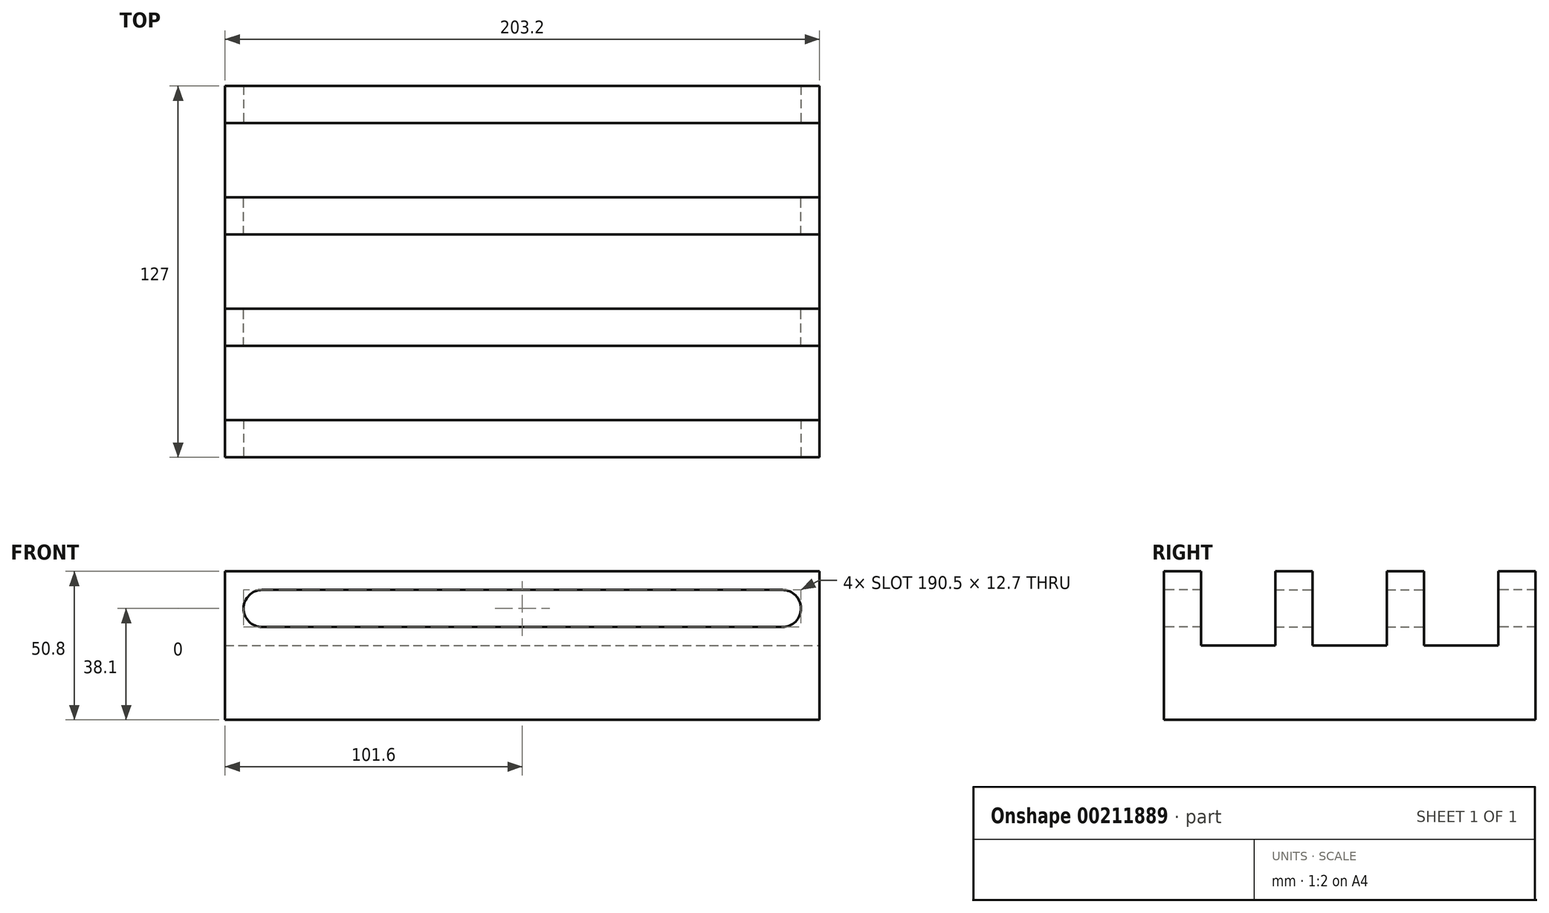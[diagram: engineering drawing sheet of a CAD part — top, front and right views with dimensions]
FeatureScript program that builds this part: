
annotation { "Feature Type Name" : "Feature", "Feature Type Description" : "" }
export const myFeature = defineFeature(function(context is Context, id is Id, definition is map)
    precondition{}
    {
        {
            var Q0;
            Q0=qCreatedBy(makeId("Top.planeOp"),FACE);
            var sketch = newSketch(context, id + "F0", { "sketchPlane" : qUnion([Q0])});
            skLineSegment(sketch, "E0.bottom", {"start": v(101.6, 63.5) * mm, "end": v(-101.6, 63.5) * mm});
            skLineSegment(sketch, "E0.top", {"start": v(101.6, -63.5) * mm, "end": v(-101.6, -63.5) * mm});
            skLineSegment(sketch, "E0.left", {"start": v(101.6, 63.5) * mm, "end": v(101.6, -63.5) * mm});
            skLineSegment(sketch, "E0.right", {"start": v(-101.6, 63.5) * mm, "end": v(-101.6, -63.5) * mm});
            skPoint(sketch, "E0.middle", {"position": v(0, 0) * mm});
            skSolve(sketch);
        }
        {
            var Q0;
            Q0 = qSketchRegion(id + "F0", true);
            extrude(context, id + "F1", {"entities" : qUnion([Q0]), "endBound" : BoundingType.SYMMETRIC, "depth" : 25.4 * mm});
        }
        {
            var Q0;
            Q0=makeQuery(id+"F1.opExtrude","CAP_FACE",FACE,{"disambiguationData":[OSD([sQuery(id+"F0.wireOp",EDGE,"E0.bottom"),sQuery(id+"F0.wireOp",EDGE,"E0.top"),sQuery(id+"F0.wireOp",EDGE,"E0.left"),sQuery(id+"F0.wireOp",EDGE,"E0.right")])],"isStart":false});
            var sketch = newSketch(context, id + "F2", { "sketchPlane" : qUnion([Q0])});
            skLineSegment(sketch, "E1.bottom", {"start": v(-101.6, 63.5) * mm, "end": v(101.6, 63.5) * mm});
            skLineSegment(sketch, "E1.top", {"start": v(-101.6, 50.8) * mm, "end": v(101.6, 50.8) * mm});
            skLineSegment(sketch, "E1.left", {"start": v(-101.6, 63.5) * mm, "end": v(-101.6, 50.8) * mm});
            skLineSegment(sketch, "E1.right", {"start": v(101.6, 63.5) * mm, "end": v(101.6, 50.8) * mm});
            skLineSegment(sketch, "E2.MirrorCS", {"start": v(-101.6, -50.8) * mm, "end": v(101.6, -50.8) * mm});
            skSolve(sketch);
        }
        {
            var Q0;
            Q0 = qSketchRegion(id + "F2", true);
            var Q1;
            {var subQ0=sQuery(id+"F2.wireOp",EDGE,"E2.MirrorCS");Q1=makeQuery(id+"F2.imprint","IMPRINT",FACE,{"disambiguationData":[TD([[makeQuery(id+"F2.imprint","IMPRINT",EDGE,{"derivedFrom":subQ0}),-1.0]])]});}
            extrude(context, id + "F3", {"entities" : qUnion([Q0, Q1]), "operationType" : NewBodyOperationType.ADD, "depth" : 25.4 * mm});
        }
        {
            var Q0;
            {var subQ0=sQuery(id+"F0.wireOp",EDGE,"E0.top");Q0=makeQuery(id+"F3.boolean.opBoolean","MERGE",FACE,{"derivedFrom":[makeQuery(id+"F1.opExtrude","SWEPT_FACE",FACE,{"disambiguationData":[OSD([subQ0])]}),makeQuery(id+"F3.opExtrude","SWEPT_FACE",FACE,{"disambiguationData":[OSD([subQ0])]})]});}
            var sketch = newSketch(context, id + "F4", { "sketchPlane" : qUnion([Q0])});
            skArc(sketch, "E3", {"start": v(88.9, 19.05) * mm, "mid": v(95.25, 25.4) * mm, "end": v(88.9, 31.75) * mm});
            skArc(sketch, "E4.MirrorC", {"start": v(-88.9, 19.05) * mm, "mid": v(-95.25, 25.4) * mm, "end": v(-88.9, 31.75) * mm});
            skLineSegment(sketch, "E5", {"start": v(88.9, 19.05) * mm, "end": v(-88.9, 19.05) * mm});
            skLineSegment(sketch, "E6", {"start": v(88.9, 31.75) * mm, "end": v(-88.9, 31.75) * mm});
            skSolve(sketch);
        }
        {
            var Q0;
            Q0 = qSketchRegion(id + "F4", true);
            extrude(context, id + "F5", {"entities" : qUnion([Q0]), "operationType" : NewBodyOperationType.REMOVE, "oppositeDirection" : true, "depth" : 127 * mm});
        }
        {
            var Q0;
            Q0=makeQuery(id+"F1.opExtrude","CAP_FACE",FACE,{"disambiguationData":[OSD([sQuery(id+"F0.wireOp",EDGE,"E0.bottom"),sQuery(id+"F0.wireOp",EDGE,"E0.top"),sQuery(id+"F0.wireOp",EDGE,"E0.left"),sQuery(id+"F0.wireOp",EDGE,"E0.right")])],"isStart":false});
            var sketch = newSketch(context, id + "F6", { "sketchPlane" : qUnion([Q0])});
            skLineSegment(sketch, "E7.bottom", {"start": v(-101.6, -25.4) * mm, "end": v(101.6, -25.4) * mm});
            skLineSegment(sketch, "E7.top", {"start": v(-101.6, -12.7) * mm, "end": v(101.6, -12.7) * mm});
            skLineSegment(sketch, "E7.left", {"start": v(-101.6, -25.4) * mm, "end": v(-101.6, -12.7) * mm});
            skLineSegment(sketch, "E7.right", {"start": v(101.6, -25.4) * mm, "end": v(101.6, -12.7) * mm});
            skLineSegment(sketch, "E8.bottom", {"start": v(-101.6, 12.7) * mm, "end": v(101.6, 12.7) * mm});
            skLineSegment(sketch, "E8.top", {"start": v(-101.6, 25.4) * mm, "end": v(101.6, 25.4) * mm});
            skLineSegment(sketch, "E8.left", {"start": v(-101.6, 12.7) * mm, "end": v(-101.6, 25.4) * mm});
            skLineSegment(sketch, "E8.right", {"start": v(101.6, 12.7) * mm, "end": v(101.6, 25.4) * mm});
            skSolve(sketch);
        }
        {
            var Q0;
            Q0=makeQuery(id+"F6.imprint","IMPRINT",FACE,{"disambiguationData":[TD([[makeQuery(id+"F6.imprint","IMPRINT",EDGE,{"derivedFrom":sQuery(id+"F6.wireOp",EDGE,"E8.bottom")}),1.0]])]});
            var Q1;
            Q1=makeQuery(id+"F6.imprint","IMPRINT",FACE,{"disambiguationData":[TD([[makeQuery(id+"F6.imprint","IMPRINT",EDGE,{"derivedFrom":sQuery(id+"F6.wireOp",EDGE,"E7.bottom")}),1.0]])]});
            extrude(context, id + "F7", {"entities" : qUnion([Q0, Q1]), "operationType" : NewBodyOperationType.ADD, "depth" : 25.4 * mm});
        }
        {
            var Q0;
            Q0=makeQuery(id+"F7.opExtrude","SWEPT_FACE",FACE,{"disambiguationData":[OSD([sQuery(id+"F6.wireOp",EDGE,"E8.top")])]});
            var sketch = newSketch(context, id + "F8", { "sketchPlane" : qUnion([Q0])});
            skPoint(sketch, "E9.centerSnap0", {"position": v(0, 12.7) * mm});
            skPoint(sketch, "E9.centerSnap1", {"position": v(101.6, 25.4) * mm});
            skArc(sketch, "E10", {"start": v(-88.9, 31.75) * mm, "mid": v(-95.25, 25.4) * mm, "end": v(-88.9, 19.05) * mm});
            skArc(sketch, "E11.MirrorC", {"start": v(88.9, 31.75) * mm, "mid": v(95.25, 25.4) * mm, "end": v(88.9, 19.05) * mm});
            skLineSegment(sketch, "E12", {"start": v(-88.9, 31.75) * mm, "end": v(88.9, 31.75) * mm});
            skLineSegment(sketch, "E13", {"start": v(-88.9, 19.05) * mm, "end": v(88.9, 19.05) * mm});
            skSolve(sketch);
        }
        {
            var Q0;
            Q0=makeQuery(id+"F8.imprint","IMPRINT",FACE,{"disambiguationData":[TD([[makeQuery(id+"F8.imprint","IMPRINT",EDGE,{"derivedFrom":sQuery(id+"F8.wireOp",EDGE,"E10")}),1.0]])]});
            extrude(context, id + "F9", {"entities" : qUnion([Q0]), "operationType" : NewBodyOperationType.REMOVE, "oppositeDirection" : true, "depth" : 50.8 * mm});
        }
    });
